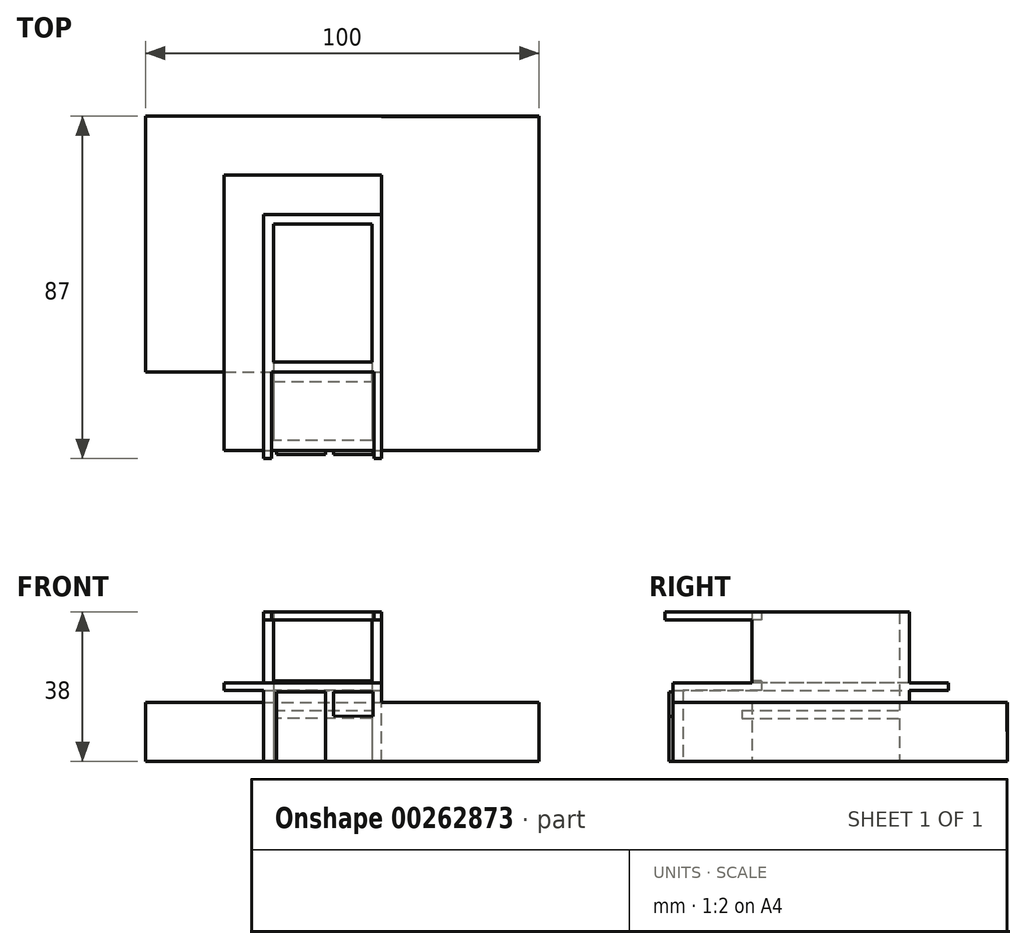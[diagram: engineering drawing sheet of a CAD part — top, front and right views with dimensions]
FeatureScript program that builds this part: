
annotation { "Feature Type Name" : "Feature", "Feature Type Description" : "" }
export const myFeature = defineFeature(function(context is Context, id is Id, definition is map)
    precondition{}
    {
        {
            var Q0;
            Q0=qCreatedBy(makeId("Top.planeOp"),FACE);
            var sketch = newSketch(context, id + "F0", { "sketchPlane" : qUnion([Q0])});
            skLineSegment(sketch, "E0.bottom", {"start": v(-15.73, 29.98) * mm, "end": v(14.27, 29.98) * mm});
            skLineSegment(sketch, "E0.top", {"start": v(-15.73, -30.02) * mm, "end": v(14.27, -30.02) * mm});
            skLineSegment(sketch, "E0.left", {"start": v(-15.73, 29.98) * mm, "end": v(-15.73, -30.02) * mm});
            skLineSegment(sketch, "E0.right", {"start": v(14.27, 29.98) * mm, "end": v(14.27, -30.02) * mm});
            skLineSegment(sketch, "E1.0", {"start": v(-13.23, 27.48) * mm, "end": v(11.77, 27.48) * mm});
            skLineSegment(sketch, "E1.1", {"start": v(-13.23, 27.48) * mm, "end": v(-13.23, -27.52) * mm});
            skLineSegment(sketch, "E1.2", {"start": v(-13.23, -27.52) * mm, "end": v(11.77, -27.52) * mm});
            skLineSegment(sketch, "E1.3", {"start": v(11.77, 27.48) * mm, "end": v(11.77, -27.52) * mm});
            skSolve(sketch);
        }
        {
            var Q0;
            Q0=makeQuery(id+"F0.imprint","IMPRINT",FACE,{"disambiguationData":[TD([[makeQuery(id+"F0.imprint","IMPRINT",EDGE,{"derivedFrom":sQuery(id+"F0.wireOp",EDGE,"E0.bottom")}),-1.0]])]});
            extrude(context, id + "F1", {"entities" : qUnion([Q0]), "depth" : 20 * mm});
        }
        {
            var Q0;
            Q0=makeQuery(id+"F1.opExtrude","SWEPT_FACE",FACE,{"disambiguationData":[OSD([sQuery(id+"F0.wireOp",EDGE,"E0.left")])]});
            var sketch = newSketch(context, id + "F2", { "sketchPlane" : qUnion([Q0])});
            skLineSegment(sketch, "E2", {"start": v(-29.98, 0) * mm, "end": v(-29.98, 15) * mm});
            skLineSegment(sketch, "E3", {"start": v(-29.98, 15) * mm, "end": v(10.02, 15) * mm});
            skLineSegment(sketch, "E4", {"start": v(10.02, 15) * mm, "end": v(10.02, 0) * mm});
            skLineSegment(sketch, "E5", {"start": v(10.02, 0) * mm, "end": v(-29.98, 0) * mm});
            skSolve(sketch);
        }
        {
            var Q0;
            Q0=makeQuery(id+"F2.imprint","IMPRINT",FACE,{"disambiguationData":[TD([[makeQuery(id+"F2.imprint","IMPRINT",EDGE,{"derivedFrom":sQuery(id+"F2.wireOp",EDGE,"E2")}),1.0]])]});
            extrude(context, id + "F3", {"entities" : qUnion([Q0]), "operationType" : NewBodyOperationType.ADD, "depth" : 30 * mm});
        }
        {
            var Q0;
            Q0=makeQuery(id+"F1.opExtrude","SWEPT_FACE",FACE,{"disambiguationData":[OSD([sQuery(id+"F0.wireOp",EDGE,"E0.top")])]});
            var sketch = newSketch(context, id + "F4", { "sketchPlane" : qUnion([Q0])});
            skLineSegment(sketch, "E6", {"start": v(-12.46, 0) * mm, "end": v(-12.46, 17.63) * mm});
            skLineSegment(sketch, "E7", {"start": v(-12.46, 17.63) * mm, "end": v(0, 17.63) * mm});
            skLineSegment(sketch, "E8", {"start": v(0, 17.63) * mm, "end": v(0, 0) * mm});
            skLineSegment(sketch, "E9", {"start": v(0, 0) * mm, "end": v(-12.46, 0) * mm});
            skLineSegment(sketch, "E10", {"start": v(12.11, 17.63) * mm, "end": v(2.03, 17.63) * mm});
            skLineSegment(sketch, "E11", {"start": v(2.03, 17.63) * mm, "end": v(2.03, 11.55) * mm});
            skLineSegment(sketch, "E12", {"start": v(12.11, 17.63) * mm, "end": v(12.11, 11.42) * mm});
            skLineSegment(sketch, "E13", {"start": v(12.11, 11.42) * mm, "end": v(2.03, 11.55) * mm});
            skSolve(sketch);
        }
        {
            var Q0;
            Q0=makeQuery(id+"F1.opExtrude","SWEPT_FACE",FACE,{"disambiguationData":[OSD([sQuery(id+"F0.wireOp",EDGE,"E0.left")])]});
            var sketch = newSketch(context, id + "F5", { "sketchPlane" : qUnion([Q0])});
            skLineSegment(sketch, "E14", {"start": v(-29.98, 20) * mm, "end": v(-29.98, 18) * mm});
            skLineSegment(sketch, "E15", {"start": v(-29.98, 20) * mm, "end": v(30.02, 20) * mm});
            skLineSegment(sketch, "E16", {"start": v(30.02, 20) * mm, "end": v(30.02, 18) * mm});
            skLineSegment(sketch, "E17", {"start": v(30.02, 18) * mm, "end": v(-29.98, 18) * mm});
            skSolve(sketch);
        }
        {
            var Q0;
            Q0=makeQuery(id+"F5.imprint","IMPRINT",FACE,{"disambiguationData":[TD([[makeQuery(id+"F5.imprint","IMPRINT",EDGE,{"derivedFrom":sQuery(id+"F5.wireOp",EDGE,"E14")}),1.0]])]});
            extrude(context, id + "F6", {"entities" : qUnion([Q0]), "operationType" : NewBodyOperationType.ADD, "depth" : 10 * mm});
        }
        {
            var Q0;
            Q0=makeQuery(id+"F6.boolean.opBoolean","MERGE",FACE,{"derivedFrom":[makeQuery(id+"F1.opExtrude","CAP_FACE",FACE,{"disambiguationData":[OSD([sQuery(id+"F0.wireOp",EDGE,"E0.bottom"),sQuery(id+"F0.wireOp",EDGE,"E0.top"),sQuery(id+"F0.wireOp",EDGE,"E0.left"),sQuery(id+"F0.wireOp",EDGE,"E0.right"),sQuery(id+"F0.wireOp",EDGE,"E1.0"),sQuery(id+"F0.wireOp",EDGE,"E1.1"),sQuery(id+"F0.wireOp",EDGE,"E1.2"),sQuery(id+"F0.wireOp",EDGE,"E1.3")])],"isStart":false}),makeQuery(id+"F6.opExtrude","SWEPT_FACE",FACE,{"disambiguationData":[OSD([sQuery(id+"F5.wireOp",EDGE,"E15")])]})]});
            var sketch = newSketch(context, id + "F7", { "sketchPlane" : qUnion([Q0])});
            skLineSegment(sketch, "E18", {"start": v(14.27, 29.98) * mm, "end": v(-15.73, 29.98) * mm});
            skLineSegment(sketch, "E19", {"start": v(-15.73, 29.98) * mm, "end": v(-15.73, -30.02) * mm});
            skLineSegment(sketch, "E20", {"start": v(-15.73, 29.98) * mm, "end": v(-15.73, -10.02) * mm});
            skLineSegment(sketch, "E21", {"start": v(-15.73, -10.02) * mm, "end": v(-13.23, -10.02) * mm});
            skLineSegment(sketch, "E22", {"start": v(14.27, 29.98) * mm, "end": v(14.27, -10.02) * mm});
            skLineSegment(sketch, "E23", {"start": v(14.27, -10.02) * mm, "end": v(11.77, -10.02) * mm});
            skSolve(sketch);
        }
        {
            var Q0;
            Q0=makeQuery(id+"F7.imprint","IMPRINT",FACE,{"disambiguationData":[TD([[makeQuery(id+"F7.imprint","IMPRINT",EDGE,{"derivedFrom":sQuery(id+"F7.wireOp",EDGE,"E18")}),-1.0]])]});
            extrude(context, id + "F8", {"entities" : qUnion([Q0]), "operationType" : NewBodyOperationType.ADD, "depth" : 18 * mm});
        }
        {
            var Q0;
            Q0=makeQuery(id+"F8.boolean.opBoolean","MERGE",FACE,{"derivedFrom":[makeQuery(id+"F6.boolean.opBoolean","MERGE",FACE,{"derivedFrom":[makeQuery(id+"F3.boolean.opBoolean","MERGE",FACE,{"derivedFrom":[makeQuery(id+"F1.opExtrude","SWEPT_FACE",FACE,{"disambiguationData":[OSD([sQuery(id+"F0.wireOp",EDGE,"E0.bottom")])]}),makeQuery(id+"F3.opExtrude","SWEPT_FACE",FACE,{"disambiguationData":[OSD([sQuery(id+"F2.wireOp",EDGE,"E2")])]})]}),makeQuery(id+"F6.opExtrude","SWEPT_FACE",FACE,{"disambiguationData":[OSD([sQuery(id+"F5.wireOp",EDGE,"E14")])]})]}),makeQuery(id+"F8.opExtrude","SWEPT_FACE",FACE,{"disambiguationData":[OSD([sQuery(id+"F7.wireOp",EDGE,"E18")])]})]});
            var sketch = newSketch(context, id + "F9", { "sketchPlane" : qUnion([Q0])});
            skLineSegment(sketch, "E24", {"start": v(45.73, 15) * mm, "end": v(-14.27, 15) * mm});
            skSolve(sketch);
        }
        {
            var Q0;
            {var subQ0=sQuery(id+"F2.wireOp",EDGE,"E2");var subQ3=makeQuery(id+"F3.opExtrude","CAP_EDGE",EDGE,{"disambiguationData":[OSD([subQ0])],"isStart":false});Q0=makeQuery(id+"F9.imprint","IMPRINT",FACE,{"disambiguationData":[TD([[makeQuery(id+"F9.imprint","IMPRINT",EDGE,{"derivedFrom":subQ3}),-1.0]])]});}
            extrude(context, id + "F10", {"entities" : qUnion([Q0]), "operationType" : NewBodyOperationType.ADD, "depth" : 25 * mm});
        }
        {
            var Q0;
            Q0=makeQuery(id+"F8.boolean.opBoolean","MERGE",FACE,{"derivedFrom":[makeQuery(id+"F6.boolean.opBoolean","MERGE",FACE,{"derivedFrom":[makeQuery(id+"F3.boolean.opBoolean","MERGE",FACE,{"derivedFrom":[makeQuery(id+"F1.opExtrude","SWEPT_FACE",FACE,{"disambiguationData":[OSD([sQuery(id+"F0.wireOp",EDGE,"E0.bottom")])]}),makeQuery(id+"F3.opExtrude","SWEPT_FACE",FACE,{"disambiguationData":[OSD([sQuery(id+"F2.wireOp",EDGE,"E2")])]})]}),makeQuery(id+"F6.opExtrude","SWEPT_FACE",FACE,{"disambiguationData":[OSD([sQuery(id+"F5.wireOp",EDGE,"E14")])]})]}),makeQuery(id+"F8.opExtrude","SWEPT_FACE",FACE,{"disambiguationData":[OSD([sQuery(id+"F7.wireOp",EDGE,"E18")])]})]});
            var sketch = newSketch(context, id + "F11", { "sketchPlane" : qUnion([Q0])});
            skLineSegment(sketch, "E25", {"start": v(25.73, 20) * mm, "end": v(-14.27, 20) * mm});
            skLineSegment(sketch, "E26", {"start": v(25.73, 18) * mm, "end": v(-14.27, 18) * mm});
            skSolve(sketch);
        }
        {
            var Q0;
            {var subQ1=sQuery(id+"F5.wireOp",EDGE,"E14");var subQ2=makeQuery(id+"F6.opExtrude","CAP_EDGE",EDGE,{"disambiguationData":[OSD([subQ1])],"isStart":false});Q0=makeQuery(id+"F11.imprint","IMPRINT",FACE,{"disambiguationData":[TD([[makeQuery(id+"F11.imprint","IMPRINT",EDGE,{"derivedFrom":subQ2}),-1.0]])]});}
            extrude(context, id + "F12", {"entities" : qUnion([Q0]), "operationType" : NewBodyOperationType.ADD, "depth" : 10 * mm});
        }
        {
            var Q0;
            Q0=makeQuery(id+"F1.opExtrude","SWEPT_FACE",FACE,{"disambiguationData":[OSD([sQuery(id+"F0.wireOp",EDGE,"E1.2")])]});
            var sketch = newSketch(context, id + "F13", { "sketchPlane" : qUnion([Q0])});
            skLineSegment(sketch, "E27", {"start": v(13.23, 20) * mm, "end": v(-11.77, 20) * mm});
            skLineSegment(sketch, "E28", {"start": v(-11.77, 20) * mm, "end": v(-11.77, 18) * mm});
            skLineSegment(sketch, "E29", {"start": v(-11.77, 18) * mm, "end": v(13.23, 18) * mm});
            skLineSegment(sketch, "E30", {"start": v(13.23, 18) * mm, "end": v(13.23, 20) * mm});
            skSolve(sketch);
        }
        {
            var Q0;
            Q0=makeQuery(id+"F13.imprint","IMPRINT",FACE,{"disambiguationData":[TD([[makeQuery(id+"F13.imprint","IMPRINT",EDGE,{"derivedFrom":sQuery(id+"F13.wireOp",EDGE,"E27")}),1.0]])]});
            extrude(context, id + "F14", {"entities" : qUnion([Q0]), "operationType" : NewBodyOperationType.ADD, "depth" : 20 * mm});
        }
        {
            var Q0;
            {var subQ0=sQuery(id+"F0.wireOp",EDGE,"E1.0");Q0=makeQuery(id+"F8.boolean.opBoolean","MERGE",FACE,{"derivedFrom":[makeQuery(id+"F1.opExtrude","SWEPT_FACE",FACE,{"disambiguationData":[OSD([subQ0])]}),makeQuery(id+"F8.opExtrude","SWEPT_FACE",FACE,{"disambiguationData":[OSD([subQ0])]})]});}
            var sketch = newSketch(context, id + "F15", { "sketchPlane" : qUnion([Q0])});
            skLineSegment(sketch, "E31", {"start": v(-13.23, 38) * mm, "end": v(-13.23, 13) * mm});
            skLineSegment(sketch, "E32", {"start": v(-13.23, 13) * mm, "end": v(11.77, 13) * mm});
            skLineSegment(sketch, "E33", {"start": v(11.77, 13) * mm, "end": v(11.77, 11) * mm});
            skLineSegment(sketch, "E34", {"start": v(11.77, 11) * mm, "end": v(-13.23, 11) * mm});
            skLineSegment(sketch, "E35", {"start": v(-13.23, 11) * mm, "end": v(-13.23, 13) * mm});
            skSolve(sketch);
        }
        {
            var Q0;
            Q0=makeQuery(id+"F15.imprint","IMPRINT",FACE,{"disambiguationData":[TD([[makeQuery(id+"F15.imprint","IMPRINT",EDGE,{"derivedFrom":sQuery(id+"F15.wireOp",EDGE,"E32")}),-1.0]])]});
            extrude(context, id + "F16", {"entities" : qUnion([Q0]), "operationType" : NewBodyOperationType.ADD, "depth" : 40 * mm});
        }
        {
            var Q0;
            {var subQ0=sQuery(id+"F7.wireOp",EDGE,"E22");var subQ1=sQuery(id+"F7.wireOp",EDGE,"E18");var subQ2=sQuery(id+"F0.wireOp",EDGE,"E0.right");var subQ3=sQuery(id+"F0.wireOp",EDGE,"E0.bottom");Q0=makeQuery(id+"F12.boolean.opBoolean","MERGE",FACE,{"derivedFrom":[makeQuery(id+"F10.boolean.opBoolean","MERGE",FACE,{"derivedFrom":[makeQuery(id+"F8.boolean.opBoolean","MERGE",FACE,{"derivedFrom":[makeQuery(id+"F1.opExtrude","SWEPT_FACE",FACE,{"disambiguationData":[OSD([subQ2])]}),makeQuery(id+"F8.opExtrude","SWEPT_FACE",FACE,{"disambiguationData":[OSD([subQ0])]})]}),makeQuery(id+"F10.opExtrude","SWEPT_FACE",FACE,{"disambiguationData":[OSD([subQ3,subQ2,subQ1,subQ0])]})]}),makeQuery(id+"F12.opExtrude","SWEPT_FACE",FACE,{"disambiguationData":[OSD([subQ3,subQ2,subQ1,subQ0])]})]});}
            var sketch = newSketch(context, id + "F17", { "sketchPlane" : qUnion([Q0])});
            skLineSegment(sketch, "E36", {"start": v(54.98, 15) * mm, "end": v(-30.02, 15) * mm});
            skLineSegment(sketch, "E37", {"start": v(-30.02, 15) * mm, "end": v(-30.02, 0) * mm});
            skLineSegment(sketch, "E38", {"start": v(-30.02, 0) * mm, "end": v(54.98, 0) * mm});
            skLineSegment(sketch, "E39", {"start": v(54.98, 0) * mm, "end": v(54.79, 15.44) * mm});
            skSolve(sketch);
        }
        {
            var Q0;
            {var subQ1=sQuery(id+"F17.wireOp",EDGE,"E37");Q0=makeQuery(id+"F17.imprint","IMPRINT",FACE,{"disambiguationData":[TD([[makeQuery(id+"F17.imprint","IMPRINT",EDGE,{"derivedFrom":subQ1}),1.0]])]});}
            extrude(context, id + "F18", {"entities" : qUnion([Q0]), "operationType" : NewBodyOperationType.ADD, "depth" : 40 * mm});
        }
        {
            var Q0;
            Q0=makeQuery(id+"F4.imprint","IMPRINT",FACE,{"disambiguationData":[TD([[makeQuery(id+"F4.imprint","IMPRINT",EDGE,{"derivedFrom":sQuery(id+"F4.wireOp",EDGE,"E6")}),-1.0]])]});
            var Q1;
            Q1=makeQuery(id+"F4.imprint","IMPRINT",FACE,{"disambiguationData":[TD([[makeQuery(id+"F4.imprint","IMPRINT",EDGE,{"derivedFrom":sQuery(id+"F4.wireOp",EDGE,"E10")}),1.0]])]});
            extrude(context, id + "F19", {"entities" : qUnion([Q0, Q1]), "operationType" : NewBodyOperationType.ADD, "depth" : 1 * mm});
        }
        {
            var Q0;
            Q0=makeQuery(id+"F14.boolean.opBoolean","MERGE",FACE,{"derivedFrom":[makeQuery(id+"F12.boolean.opBoolean","MERGE",FACE,{"derivedFrom":[makeQuery(id+"F6.boolean.opBoolean","MERGE",FACE,{"derivedFrom":[makeQuery(id+"F1.opExtrude","CAP_FACE",FACE,{"disambiguationData":[OSD([sQuery(id+"F0.wireOp",EDGE,"E0.bottom"),sQuery(id+"F0.wireOp",EDGE,"E0.top"),sQuery(id+"F0.wireOp",EDGE,"E0.left"),sQuery(id+"F0.wireOp",EDGE,"E0.right"),sQuery(id+"F0.wireOp",EDGE,"E1.0"),sQuery(id+"F0.wireOp",EDGE,"E1.1"),sQuery(id+"F0.wireOp",EDGE,"E1.2"),sQuery(id+"F0.wireOp",EDGE,"E1.3")])],"isStart":false}),makeQuery(id+"F6.opExtrude","SWEPT_FACE",FACE,{"disambiguationData":[OSD([sQuery(id+"F5.wireOp",EDGE,"E15")])]})]}),makeQuery(id+"F12.opExtrude","SWEPT_FACE",FACE,{"disambiguationData":[OSD([sQuery(id+"F11.wireOp",EDGE,"E25")])]})]}),makeQuery(id+"F14.opExtrude","SWEPT_FACE",FACE,{"disambiguationData":[OSD([sQuery(id+"F13.wireOp",EDGE,"E27")])]})]});
            var sketch = newSketch(context, id + "F20", { "sketchPlane" : qUnion([Q0])});
            skLineSegment(sketch, "E40", {"start": v(11.77, -7.52) * mm, "end": v(11.77, -10.02) * mm});
            skLineSegment(sketch, "E41", {"start": v(11.77, -10.02) * mm, "end": v(-13.23, -10.02) * mm});
            skLineSegment(sketch, "E42", {"start": v(-13.23, -10.02) * mm, "end": v(-13.23, -7.52) * mm});
            skSolve(sketch);
        }
        {
            var Q0;
            Q0=makeQuery(id+"F20.imprint","IMPRINT",FACE,{"disambiguationData":[TD([[makeQuery(id+"F20.imprint","IMPRINT",EDGE,{"derivedFrom":sQuery(id+"F20.wireOp",EDGE,"E40")}),-1.0]])]});
            extrude(context, id + "F21", {"entities" : qUnion([Q0]), "operationType" : NewBodyOperationType.ADD, "depth" : 0.5 * mm});
        }
        {
            var Q0;
            Q0=makeQuery(id+"F21.boolean.opBoolean","MERGE",FACE,{"derivedFrom":[makeQuery(id+"F8.opExtrude","SWEPT_FACE",FACE,{"disambiguationData":[OSD([sQuery(id+"F7.wireOp",EDGE,"E21")])]}),makeQuery(id+"F8.opExtrude","SWEPT_FACE",FACE,{"disambiguationData":[OSD([sQuery(id+"F7.wireOp",EDGE,"E23")])]}),makeQuery(id+"F21.opExtrude","SWEPT_FACE",FACE,{"disambiguationData":[OSD([sQuery(id+"F20.wireOp",EDGE,"E41")])]})]});
            var sketch = newSketch(context, id + "F22", { "sketchPlane" : qUnion([Q0])});
            skLineSegment(sketch, "E43", {"start": v(-15.73, 38) * mm, "end": v(-15.73, 36) * mm});
            skLineSegment(sketch, "E44", {"start": v(-15.73, 38) * mm, "end": v(-13.73, 38) * mm});
            skLineSegment(sketch, "E45", {"start": v(14.27, 38) * mm, "end": v(12.27, 38) * mm});
            skLineSegment(sketch, "E46", {"start": v(14.27, 38) * mm, "end": v(14.27, 36) * mm});
            skLineSegment(sketch, "E47", {"start": v(-15.73, 36) * mm, "end": v(-13.73, 36) * mm});
            skLineSegment(sketch, "E48", {"start": v(-13.73, 36) * mm, "end": v(-13.73, 38) * mm});
            skLineSegment(sketch, "E49", {"start": v(12.27, 38) * mm, "end": v(12.27, 36) * mm});
            skLineSegment(sketch, "E50", {"start": v(12.27, 36) * mm, "end": v(14.27, 36) * mm});
            skSolve(sketch);
        }
        {
            var Q0;
            Q0=makeQuery(id+"F22.imprint","IMPRINT",FACE,{"disambiguationData":[TD([[makeQuery(id+"F22.imprint","IMPRINT",EDGE,{"derivedFrom":sQuery(id+"F22.wireOp",EDGE,"E45")}),1.0]])]});
            var Q1;
            Q1=makeQuery(id+"F22.imprint","IMPRINT",FACE,{"disambiguationData":[TD([[makeQuery(id+"F22.imprint","IMPRINT",EDGE,{"derivedFrom":sQuery(id+"F22.wireOp",EDGE,"E43")}),1.0]])]});
            extrude(context, id + "F23", {"entities" : qUnion([Q0, Q1]), "operationType" : NewBodyOperationType.ADD, "depth" : 22 * mm});
        }
        {
            var Q0;
            Q0=makeQuery(id+"F14.boolean.opBoolean","MERGE",FACE,{"derivedFrom":[makeQuery(id+"F12.boolean.opBoolean","MERGE",FACE,{"derivedFrom":[makeQuery(id+"F6.boolean.opBoolean","MERGE",FACE,{"derivedFrom":[makeQuery(id+"F1.opExtrude","CAP_FACE",FACE,{"disambiguationData":[OSD([sQuery(id+"F0.wireOp",EDGE,"E0.bottom"),sQuery(id+"F0.wireOp",EDGE,"E0.top"),sQuery(id+"F0.wireOp",EDGE,"E0.left"),sQuery(id+"F0.wireOp",EDGE,"E0.right"),sQuery(id+"F0.wireOp",EDGE,"E1.0"),sQuery(id+"F0.wireOp",EDGE,"E1.1"),sQuery(id+"F0.wireOp",EDGE,"E1.2"),sQuery(id+"F0.wireOp",EDGE,"E1.3")])],"isStart":false}),makeQuery(id+"F6.opExtrude","SWEPT_FACE",FACE,{"disambiguationData":[OSD([sQuery(id+"F5.wireOp",EDGE,"E15")])]})]}),makeQuery(id+"F12.opExtrude","SWEPT_FACE",FACE,{"disambiguationData":[OSD([sQuery(id+"F11.wireOp",EDGE,"E25")])]})]}),makeQuery(id+"F14.opExtrude","SWEPT_FACE",FACE,{"disambiguationData":[OSD([sQuery(id+"F13.wireOp",EDGE,"E27")])]})]});
            var sketch = newSketch(context, id + "F24", { "sketchPlane" : qUnion([Q0])});
            skLineSegment(sketch, "E51", {"start": v(14.27, -30.02) * mm, "end": v(14.27, -28.02) * mm});
            skLineSegment(sketch, "E52", {"start": v(14.27, -30.02) * mm, "end": v(12.27, -30.02) * mm});
            skLineSegment(sketch, "E53", {"start": v(-15.73, -10.02) * mm, "end": v(-15.73, -30.02) * mm});
            skLineSegment(sketch, "E54", {"start": v(-15.73, -30.02) * mm, "end": v(-13.73, -30.02) * mm});
            skLineSegment(sketch, "E55", {"start": v(-15.73, -30.02) * mm, "end": v(-15.73, -28.02) * mm});
            skLineSegment(sketch, "E56", {"start": v(-15.73, -28.02) * mm, "end": v(-15.73, -30.02) * mm});
            skLineSegment(sketch, "E57", {"start": v(-13.73, -30.02) * mm, "end": v(-13.73, -27.92) * mm});
            skLineSegment(sketch, "E58", {"start": v(-13.73, -27.92) * mm, "end": v(-15.73, -28.02) * mm});
            skLineSegment(sketch, "E59", {"start": v(12.23, -28.02) * mm, "end": v(12.27, -30.02) * mm});
            skLineSegment(sketch, "E60", {"start": v(12.23, -28.02) * mm, "end": v(14.27, -28.02) * mm});
            skLineSegment(sketch, "E61", {"start": v(12.27, -30.02) * mm, "end": v(14.27, -30.02) * mm});
            skSolve(sketch);
        }
        {
            var Q0;
            Q0=sQuery(id+"F24.wireOp",EDGE,"E58");
            var Q1;
            Q1=sQuery(id+"F24.wireOp",EDGE,"E54");
            var Q2;
            Q2=sQuery(id+"F24.wireOp",EDGE,"E57");
            var Q3;
            Q3=sQuery(id+"F24.wireOp",EDGE,"E56");
            var Q4;
            Q4=sQuery(id+"F24.wireOp",EDGE,"E60");
            var Q5;
            Q5=sQuery(id+"F24.wireOp",EDGE,"E59");
            var Q6;
            Q6=sQuery(id+"F24.wireOp",EDGE,"E52");
            var Q7;
            Q7=sQuery(id+"F24.wireOp",EDGE,"E51");
            extrude(context, id + "F25", {"bodyType" : ToolBodyType.SURFACE, "surfaceEntities" : qUnion([Q0, Q1, Q2, Q3, Q4, Q5, Q6, Q7]), "depth" : 16 * mm});
        }
        {
            var Q0;
            {var subQ0=sQuery(id+"F0.wireOp",EDGE,"E1.3");Q0=makeQuery(id+"F8.boolean.opBoolean","MERGE",FACE,{"derivedFrom":[makeQuery(id+"F1.opExtrude","SWEPT_FACE",FACE,{"disambiguationData":[OSD([subQ0])]}),makeQuery(id+"F8.opExtrude","SWEPT_FACE",FACE,{"disambiguationData":[OSD([subQ0])]})]});}
            var sketch = newSketch(context, id + "F26", { "sketchPlane" : qUnion([Q0])});
            skLineSegment(sketch, "E62", {"start": v(10.02, 38) * mm, "end": v(7.52, 38) * mm});
            skLineSegment(sketch, "E63", {"start": v(10.02, 38) * mm, "end": v(10.02, 36) * mm});
            skLineSegment(sketch, "E64", {"start": v(7.52, 38) * mm, "end": v(7.52, 36) * mm});
            skLineSegment(sketch, "E65", {"start": v(7.52, 36) * mm, "end": v(10.02, 36) * mm});
            skSolve(sketch);
        }
        {
            var Q0;
            Q0=makeQuery(id+"F26.imprint","IMPRINT",FACE,{"disambiguationData":[TD([[makeQuery(id+"F26.imprint","IMPRINT",EDGE,{"derivedFrom":sQuery(id+"F26.wireOp",EDGE,"E62")}),-1.0]])]});
            extrude(context, id + "F27", {"entities" : qUnion([Q0]), "operationType" : NewBodyOperationType.ADD, "depth" : 25 * mm});
        }
    });
